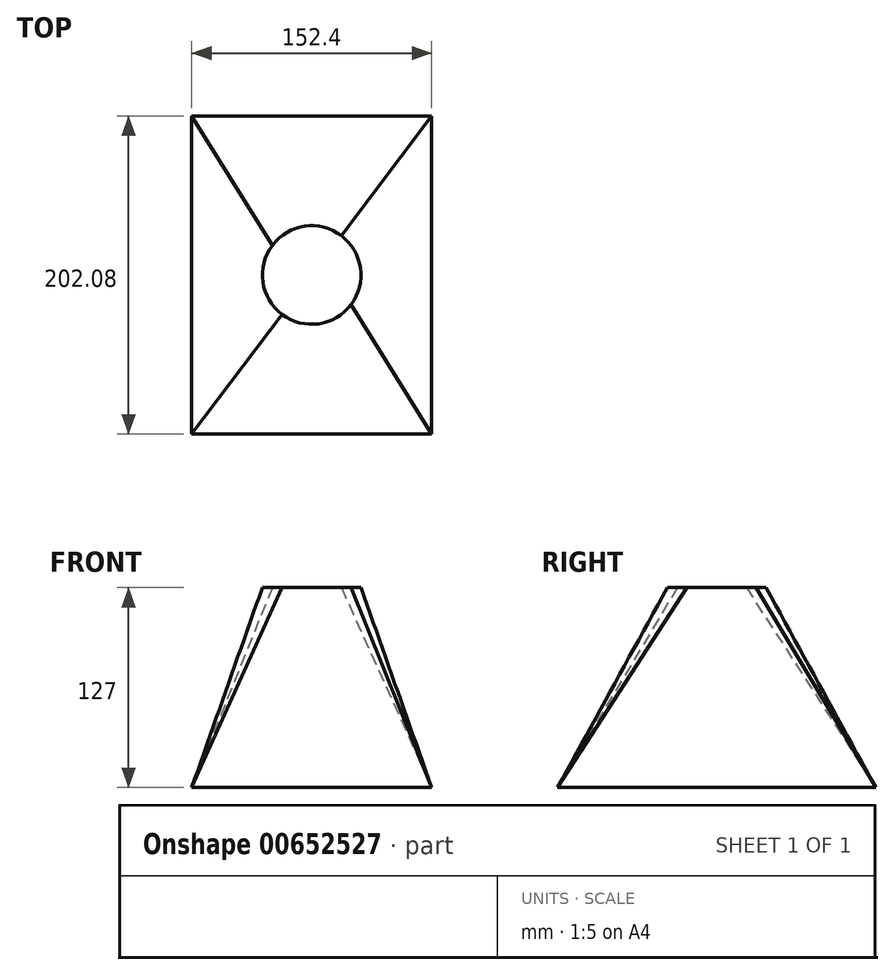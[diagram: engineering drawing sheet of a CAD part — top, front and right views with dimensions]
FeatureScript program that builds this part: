
annotation { "Feature Type Name" : "Feature", "Feature Type Description" : "" }
export const myFeature = defineFeature(function(context is Context, id is Id, definition is map)
    precondition{}
    {
        {
            var Q0;
            Q0=qCreatedBy(makeId("Top.planeOp"),FACE);
            var sketch = newSketch(context, id + "F0", { "sketchPlane" : qUnion([Q0])});
            skLineSegment(sketch, "E0.bottom", {"start": v(76.2, 101.04) * mm, "end": v(-76.2, 101.04) * mm});
            skLineSegment(sketch, "E0.top", {"start": v(76.2, -101.04) * mm, "end": v(-76.2, -101.04) * mm});
            skLineSegment(sketch, "E0.left", {"start": v(76.2, 101.04) * mm, "end": v(76.2, -101.04) * mm});
            skLineSegment(sketch, "E0.right", {"start": v(-76.2, 101.04) * mm, "end": v(-76.2, -101.04) * mm});
            skPoint(sketch, "E0.middle", {"position": v(0, 0) * mm});
            skSolve(sketch);
        }
        {
            var Q0;
            Q0=qCreatedBy(makeId("Top.planeOp"),FACE);
            cPlane(context, id + "F1", {"entities" : qUnion([Q0]), "cplaneType" : CPlaneType.OFFSET, "offset" : 127 * mm, "width" : 152.4 * mm, "height" : 152.4 * mm});
        }
        {
            var Q0;
            Q0=qCreatedBy(id+"F1.planeOp",FACE);
            var sketch = newSketch(context, id + "F2", { "sketchPlane" : qUnion([Q0])});
            skPoint(sketch, "E1.middle", {"position": v(0, 0) * mm});
            skCircle(sketch, "E2", {"center": v(0, 0) * mm, "radius": 31.3 * mm});
            skSolve(sketch);
        }
        {
            var Q0;
            Q0=makeQuery(id+"F2.imprint","IMPRINT",FACE,{"disambiguationData":[TD([[makeQuery(id+"F2.imprint","IMPRINT",EDGE,{"derivedFrom":sQuery(id+"F2.wireOp",EDGE,"E2")}),1.0]])]});
            var Q1;
            Q1=makeQuery(id+"F0.imprint","IMPRINT",FACE,{"disambiguationData":[TD([[makeQuery(id+"F0.imprint","IMPRINT",EDGE,{"derivedFrom":sQuery(id+"F0.wireOp",EDGE,"E0.bottom")}),1.0]])]});
            loft(context, id + "F3", {"sheetProfilesArray" : [{ "sheetProfileEntities" : qUnion([Q0]) }, { "sheetProfileEntities" : qUnion([Q1]) }]});
        }
    });
